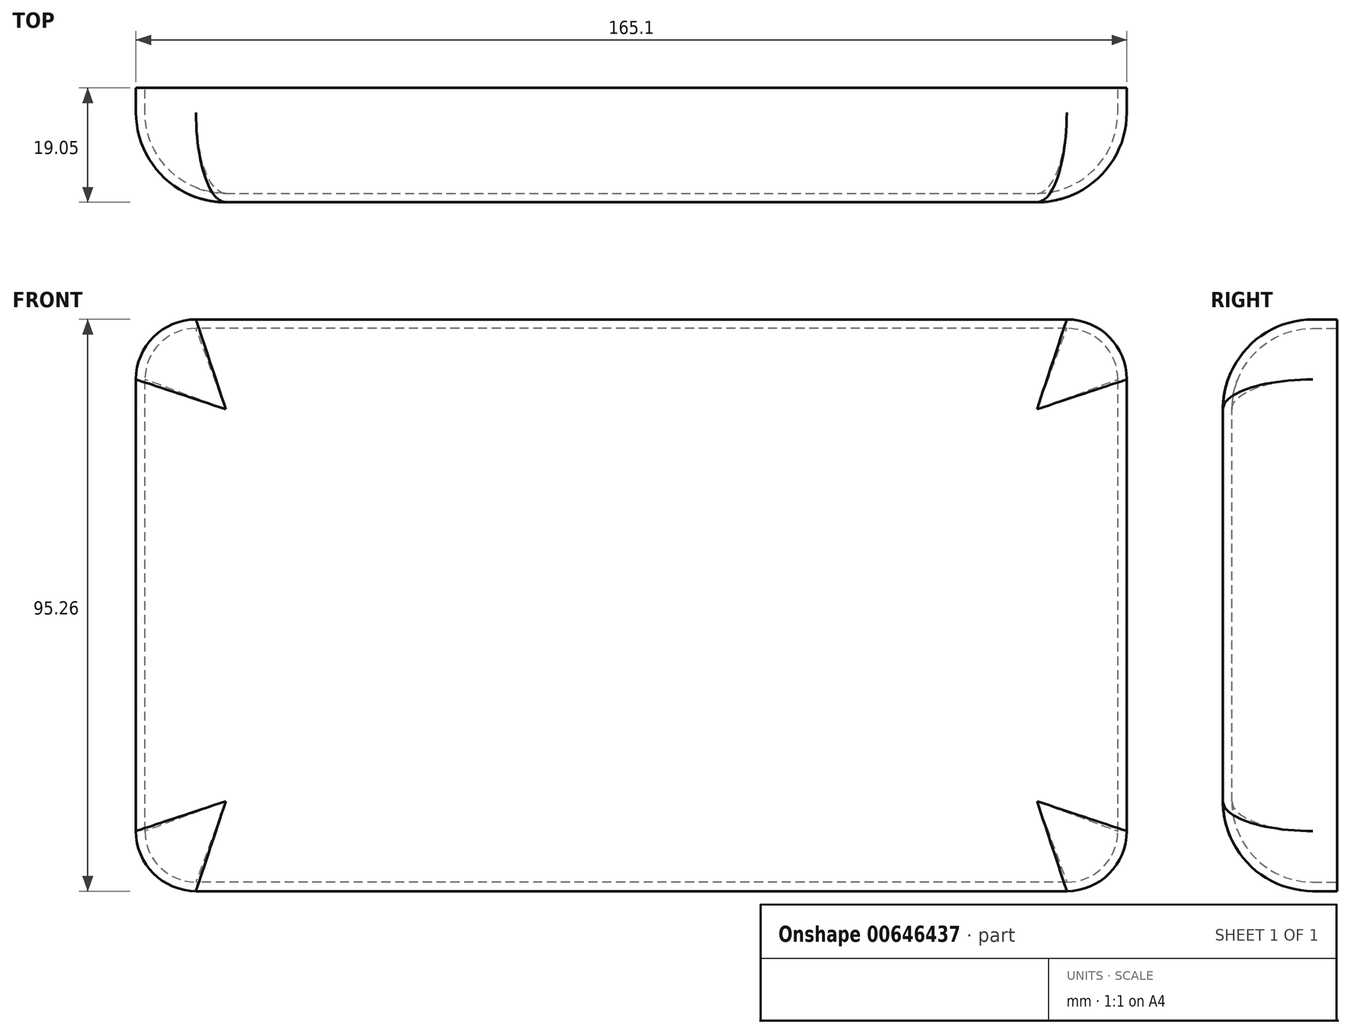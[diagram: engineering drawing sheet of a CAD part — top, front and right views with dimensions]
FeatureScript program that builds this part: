
annotation { "Feature Type Name" : "Feature", "Feature Type Description" : "" }
export const myFeature = defineFeature(function(context is Context, id is Id, definition is map)
    precondition{}
    {
        {
            var Q0;
            Q0=qCreatedBy(makeId("Front.planeOp"),FACE);
            var sketch = newSketch(context, id + "F0", { "sketchPlane" : qUnion([Q0])});
            skLineSegment(sketch, "E0.bottom", {"start": v(82.55, -47.62) * mm, "end": v(-82.55, -47.63) * mm});
            skLineSegment(sketch, "E0.top", {"start": v(82.55, 47.63) * mm, "end": v(-82.55, 47.62) * mm});
            skLineSegment(sketch, "E0.left", {"start": v(82.55, -47.62) * mm, "end": v(82.55, 47.63) * mm});
            skLineSegment(sketch, "E0.right", {"start": v(-82.55, -47.63) * mm, "end": v(-82.55, 47.62) * mm});
            skPoint(sketch, "E0.middle", {"position": v(0, 0) * mm});
            skSolve(sketch);
        }
        {
            var Q0;
            Q0=makeQuery(id+"F0.imprint","IMPRINT",FACE,{"disambiguationData":[TD([[makeQuery(id+"F0.imprint","IMPRINT",EDGE,{"derivedFrom":sQuery(id+"F0.wireOp",EDGE,"E0.bottom")}),-1.0]])]});
            extrude(context, id + "F1", {"entities" : qUnion([Q0]), "depth" : 19.05 * mm, "offsetDistance" : 25 * mm});
        }
        {
            var Q0;
            Q0=makeQuery(id+"F1.opExtrude","SWEPT_EDGE",EDGE,{"disambiguationData":[OSD([sQuery(id+"F0.wireOp",EDGE,"E0.top"),sQuery(id+"F0.wireOp",EDGE,"E0.left")])]});
            var Q1;
            Q1=makeQuery(id+"F1.opExtrude","SWEPT_EDGE",EDGE,{"disambiguationData":[OSD([sQuery(id+"F0.wireOp",EDGE,"E0.bottom"),sQuery(id+"F0.wireOp",EDGE,"E0.left")])]});
            var Q2;
            Q2=makeQuery(id+"F1.opExtrude","SWEPT_EDGE",EDGE,{"disambiguationData":[OSD([sQuery(id+"F0.wireOp",EDGE,"E0.top"),sQuery(id+"F0.wireOp",EDGE,"E0.right")])]});
            var Q3;
            Q3=makeQuery(id+"F1.opExtrude","SWEPT_EDGE",EDGE,{"disambiguationData":[OSD([sQuery(id+"F0.wireOp",EDGE,"E0.bottom"),sQuery(id+"F0.wireOp",EDGE,"E0.right")])]});
            fillet(context, id + "F2", {"entities" : qUnion([Q0, Q1, Q2, Q3]), "radius" : 10 * mm, "tangentPropagation" : true, "allowEdgeOverflow" : false});
        }
        {
            var Q0;
            Q0=makeQuery(id+"F1.opExtrude","CAP_EDGE",EDGE,{"disambiguationData":[OSD([sQuery(id+"F0.wireOp",EDGE,"E0.top")])],"isStart":false});
            var Q1;
            {var subQ0=sQuery(id+"F0.wireOp",EDGE,"E0.left");var subQ1=sQuery(id+"F0.wireOp",EDGE,"E0.top");Q1=makeQuery(id+"F2.opFillet","BLEND_EDGE",EDGE,{"blendedFrom":[makeQuery(id+"F1.opExtrude","SWEPT_EDGE",EDGE,{"disambiguationData":[OSD([subQ1,subQ0])]}),makeQuery(id+"F1.opExtrude","CAP_FACE",FACE,{"disambiguationData":[OSD([sQuery(id+"F0.wireOp",EDGE,"E0.bottom"),subQ1,subQ0,sQuery(id+"F0.wireOp",EDGE,"E0.right")])],"isStart":false})],"blendedInto":[makeQuery(id+"F1.opExtrude","CAP_FACE",FACE,{"disambiguationData":[OSD([sQuery(id+"F0.wireOp",EDGE,"E0.bottom"),subQ1,subQ0,sQuery(id+"F0.wireOp",EDGE,"E0.right")])],"isStart":false})]});}
            var Q2;
            Q2=makeQuery(id+"F1.opExtrude","CAP_EDGE",EDGE,{"disambiguationData":[OSD([sQuery(id+"F0.wireOp",EDGE,"E0.left")])],"isStart":false});
            var Q3;
            {var subQ0=sQuery(id+"F0.wireOp",EDGE,"E0.right");var subQ1=sQuery(id+"F0.wireOp",EDGE,"E0.top");Q3=makeQuery(id+"F2.opFillet","BLEND_EDGE",EDGE,{"blendedFrom":[makeQuery(id+"F1.opExtrude","SWEPT_EDGE",EDGE,{"disambiguationData":[OSD([subQ1,subQ0])]}),makeQuery(id+"F1.opExtrude","CAP_FACE",FACE,{"disambiguationData":[OSD([sQuery(id+"F0.wireOp",EDGE,"E0.bottom"),subQ1,sQuery(id+"F0.wireOp",EDGE,"E0.left"),subQ0])],"isStart":false})],"blendedInto":[makeQuery(id+"F1.opExtrude","CAP_FACE",FACE,{"disambiguationData":[OSD([sQuery(id+"F0.wireOp",EDGE,"E0.bottom"),subQ1,sQuery(id+"F0.wireOp",EDGE,"E0.left"),subQ0])],"isStart":false})]});}
            var Q4;
            Q4=makeQuery(id+"F1.opExtrude","CAP_EDGE",EDGE,{"disambiguationData":[OSD([sQuery(id+"F0.wireOp",EDGE,"E0.right")])],"isStart":false});
            var Q5;
            {var subQ0=sQuery(id+"F0.wireOp",EDGE,"E0.right");var subQ1=sQuery(id+"F0.wireOp",EDGE,"E0.bottom");Q5=makeQuery(id+"F2.opFillet","BLEND_EDGE",EDGE,{"blendedFrom":[makeQuery(id+"F1.opExtrude","SWEPT_EDGE",EDGE,{"disambiguationData":[OSD([subQ1,subQ0])]}),makeQuery(id+"F1.opExtrude","CAP_FACE",FACE,{"disambiguationData":[OSD([subQ1,sQuery(id+"F0.wireOp",EDGE,"E0.top"),sQuery(id+"F0.wireOp",EDGE,"E0.left"),subQ0])],"isStart":false})],"blendedInto":[makeQuery(id+"F1.opExtrude","CAP_FACE",FACE,{"disambiguationData":[OSD([subQ1,sQuery(id+"F0.wireOp",EDGE,"E0.top"),sQuery(id+"F0.wireOp",EDGE,"E0.left"),subQ0])],"isStart":false})]});}
            var Q6;
            Q6=makeQuery(id+"F1.opExtrude","CAP_EDGE",EDGE,{"disambiguationData":[OSD([sQuery(id+"F0.wireOp",EDGE,"E0.bottom")])],"isStart":false});
            var Q7;
            {var subQ0=sQuery(id+"F0.wireOp",EDGE,"E0.left");var subQ1=sQuery(id+"F0.wireOp",EDGE,"E0.bottom");Q7=makeQuery(id+"F2.opFillet","BLEND_EDGE",EDGE,{"blendedFrom":[makeQuery(id+"F1.opExtrude","SWEPT_EDGE",EDGE,{"disambiguationData":[OSD([subQ1,subQ0])]}),makeQuery(id+"F1.opExtrude","CAP_FACE",FACE,{"disambiguationData":[OSD([subQ1,sQuery(id+"F0.wireOp",EDGE,"E0.top"),subQ0,sQuery(id+"F0.wireOp",EDGE,"E0.right")])],"isStart":false})],"blendedInto":[makeQuery(id+"F1.opExtrude","CAP_FACE",FACE,{"disambiguationData":[OSD([subQ1,sQuery(id+"F0.wireOp",EDGE,"E0.top"),subQ0,sQuery(id+"F0.wireOp",EDGE,"E0.right")])],"isStart":false})]});}
            fillet(context, id + "F3", {"entities" : qUnion([Q0, Q1, Q2, Q3, Q4, Q5, Q6, Q7]), "radius" : 14.97 * mm, "tangentPropagation" : true, "allowEdgeOverflow" : false});
        }
        {
            var Q0;
            Q0=makeQuery(id+"F1.opExtrude","CAP_FACE",FACE,{"disambiguationData":[OSD([sQuery(id+"F0.wireOp",EDGE,"E0.bottom"),sQuery(id+"F0.wireOp",EDGE,"E0.top"),sQuery(id+"F0.wireOp",EDGE,"E0.left"),sQuery(id+"F0.wireOp",EDGE,"E0.right")])],"isStart":true});
            shell(context, id + "F4", {"entities" : qUnion([Q0]), "thickness" : 1.5 * mm});
        }
    });
